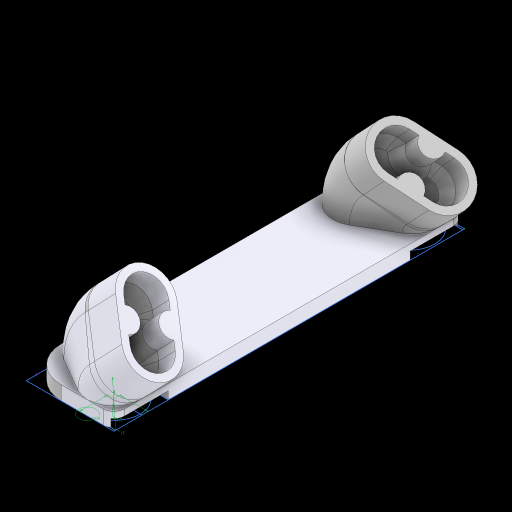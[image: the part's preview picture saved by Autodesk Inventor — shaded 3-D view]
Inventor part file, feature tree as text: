
AUTODESK INVENTOR PART (.ipt)
format: ipt  version: 2023 (Build 270158000, 158)  size: 388,096 bytes
history: native  units: mm
features: sketch x5, extrude x4, fillet x2, plane x1, sweep x1, revolve x1, chamfer x1, mirror x1
ambient origin geometry x8: Origin, YZ Plane, XZ Plane, XY Plane, X Axis, Y Axis, Z Axis, Center Point
bodies: Solid1 (feature_tree)
feature tree (16):
  sketch  "Sketch1"  dims[d0=100.0mm d1=25.0mm d2=7.5mm d3=7.5mm d4=60.0deg d5=15.0mm d6=11.0mm d7=11.0mm d8=15.0mm d11=135.0deg]
  plane  "Work Plane1"
  sweep  "Sweep1"
  extrude  "Extrusion1"  Depth=4.0mm TaperAngle=0.0deg
  fillet  "Fillet1"  Radius=3.0mm
  revolve  "Revolution1"  Angle=45.0deg
  extrude  "Extrusion4"  TaperAngle=45.0deg  [1 undecoded]
  chamfer  "Chamfer3"  Distance=10.0mm
  mirror  "Mirror3"
  sketch  "Sketch7"  dims[d33=10.0mm d34=10.0mm d35=45.0deg d37=10.0mm d38=0.959931mm d57=15.0mm d60=5.5mm d61=5.5mm d63=11.0mm d64=11.0mm d65=2.0mm d66=6.5mm d67=6.5mm d68=10.0mm d69=0.0mm d70=2.0mm d71=4.0mm d72=45.0deg d73=8.0mm d74=8.0mm d75=15.0mm d76=5.7mm d77=0.0mm d78=2.2mm d79=0.0mm d80=7.5mm d81=0.0mm d82=10.0mm]
  extrude  "Extrusion5"  TaperAngle=45.0deg  [1 undecoded]
  extrude  "Extrusion6"  Depth=10.0mm
  fillet  "Fillet2"  Radius=0.959931mm
  sketch  "Sketch3"  dims[d12=0.0mm d13=0.0mm d14=4.0mm d15=0.0mm d28=3.0mm]
  sketch  "Sketch5"  dims[d29=11.389087mm d30=45.0deg]
  sketch  "Sketch6"  dims[d31=10.0mm d32=45.0deg]
note: 2 required parameter values undecoded (feature->parameter linkage not recoverable at this tier; creation-order binding heuristic only, values carry confidence <= 0.55)
